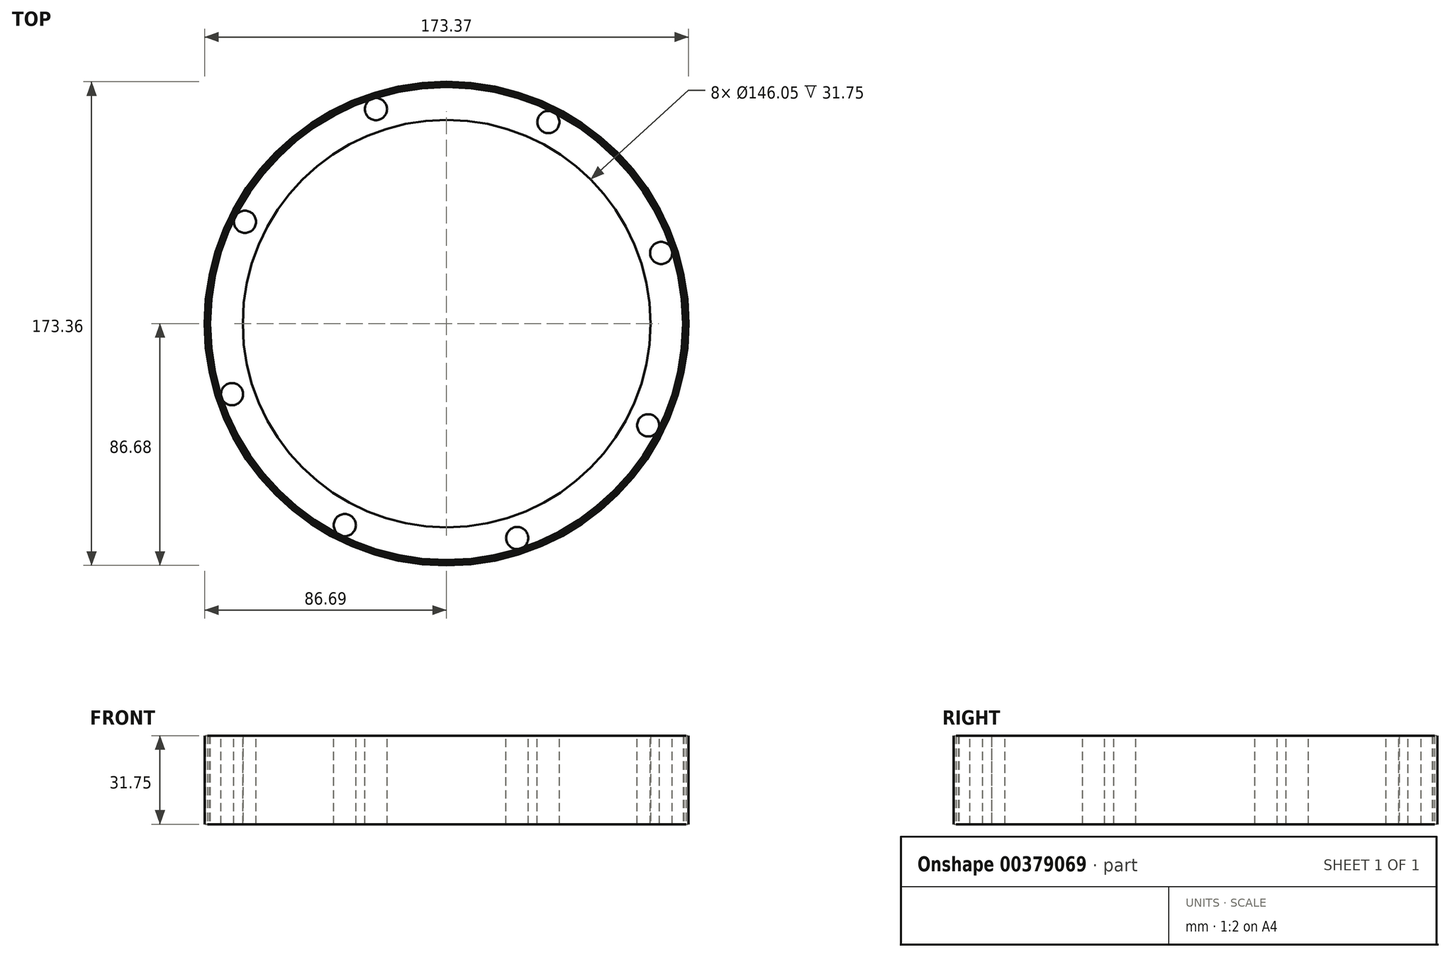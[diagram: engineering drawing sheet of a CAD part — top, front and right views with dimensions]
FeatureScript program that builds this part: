
annotation { "Feature Type Name" : "Feature", "Feature Type Description" : "" }
export const myFeature = defineFeature(function(context is Context, id is Id, definition is map)
    precondition{}
    {
        {
            var Q0;
            Q0=qCreatedBy(makeId("Top.planeOp"),FACE);
            var sketch = newSketch(context, id + "F0", { "sketchPlane" : qUnion([Q0])});
            skCircle(sketch, "E0", {"center": v(-65.5, 0) * mm, "radius": 85.73 * mm});
            skSolve(sketch);
        }
        {
            var Q0;
            Q0=makeQuery(id+"F0.imprint","IMPRINT",FACE,{"disambiguationData":[TD([[makeQuery(id+"F0.imprint","IMPRINT",EDGE,{"derivedFrom":sQuery(id+"F0.wireOp",EDGE,"E0")}),1.0]])]});
            var sketch = newSketch(context, id + "F1", { "sketchPlane" : qUnion([Q0])});
            skCircle(sketch, "E1", {"center": v(-64.53, 0) * mm, "radius": 73.03 * mm});
            skSolve(sketch);
        }
        {
            var Q0;
            Q0=makeQuery(id+"F1.imprint","IMPRINT",FACE,{"disambiguationData":[TD([[makeQuery(id+"F1.imprint","IMPRINT",EDGE,{"derivedFrom":sQuery(id+"F1.wireOp",EDGE,"E1")}),-1.0]])]});
            extrude(context, id + "F2", {"entities" : qUnion([Q0]), "depth" : 31.75 * mm});
        }
        {
            var Q0;
            Q0=makeQuery(id+"F2.opExtrude","CAP_FACE",FACE,{"disambiguationData":[OSD([sQuery(id+"F0.wireOp",EDGE,"E0"),sQuery(id+"F1.wireOp",EDGE,"E1")])],"isStart":false});
            var sketch = newSketch(context, id + "F3", { "sketchPlane" : qUnion([Q0])});
            skCircle(sketch, "E2", {"center": v(-128.48, -41.92) * mm, "radius": 2.98 * mm});
            skSolve(sketch);
        }
        {
            var Q0;
            Q0=makeQuery(id+"F3.imprint","IMPRINT",FACE,{"disambiguationData":[TD([[makeQuery(id+"F3.imprint","IMPRINT",EDGE,{"derivedFrom":sQuery(id+"F3.wireOp",EDGE,"E2")}),-1.0]])]});
            var sketch = newSketch(context, id + "F4", { "sketchPlane" : qUnion([Q0])});
            skCircle(sketch, "E3", {"center": v(-141.4, -25.3) * mm, "radius": 3.97 * mm});
            skSolve(sketch);
        }
        {
            var Q0;
            Q0 = qSketchRegion(id + "F4", true);
            extrude(context, id + "F5", {"entities" : qUnion([Q0]), "operationType" : NewBodyOperationType.REMOVE, "oppositeDirection" : true, "depth" : 38.1 * mm});
        }
        {
            var Q0;
            Q0=makeQuery(id+"F2.opExtrude","SWEPT_BODY",BODY,{"disambiguationData":[OSD([sQuery(id+"F0.wireOp",EDGE,"E0"),sQuery(id+"F1.wireOp",EDGE,"E1")])]});
            var Q1;
            Q1=makeQuery(id+"F2.opExtrude","SWEPT_FACE",FACE,{"disambiguationData":[OSD([sQuery(id+"F1.wireOp",EDGE,"E1")])]});
            circularPattern(context, id + "F6", {"entities" : qUnion([Q0]), "axis" : qUnion([Q1]), "angle" : 360 * degree, "instanceCount" : 8, "equalSpace" : true});
        }
    });
